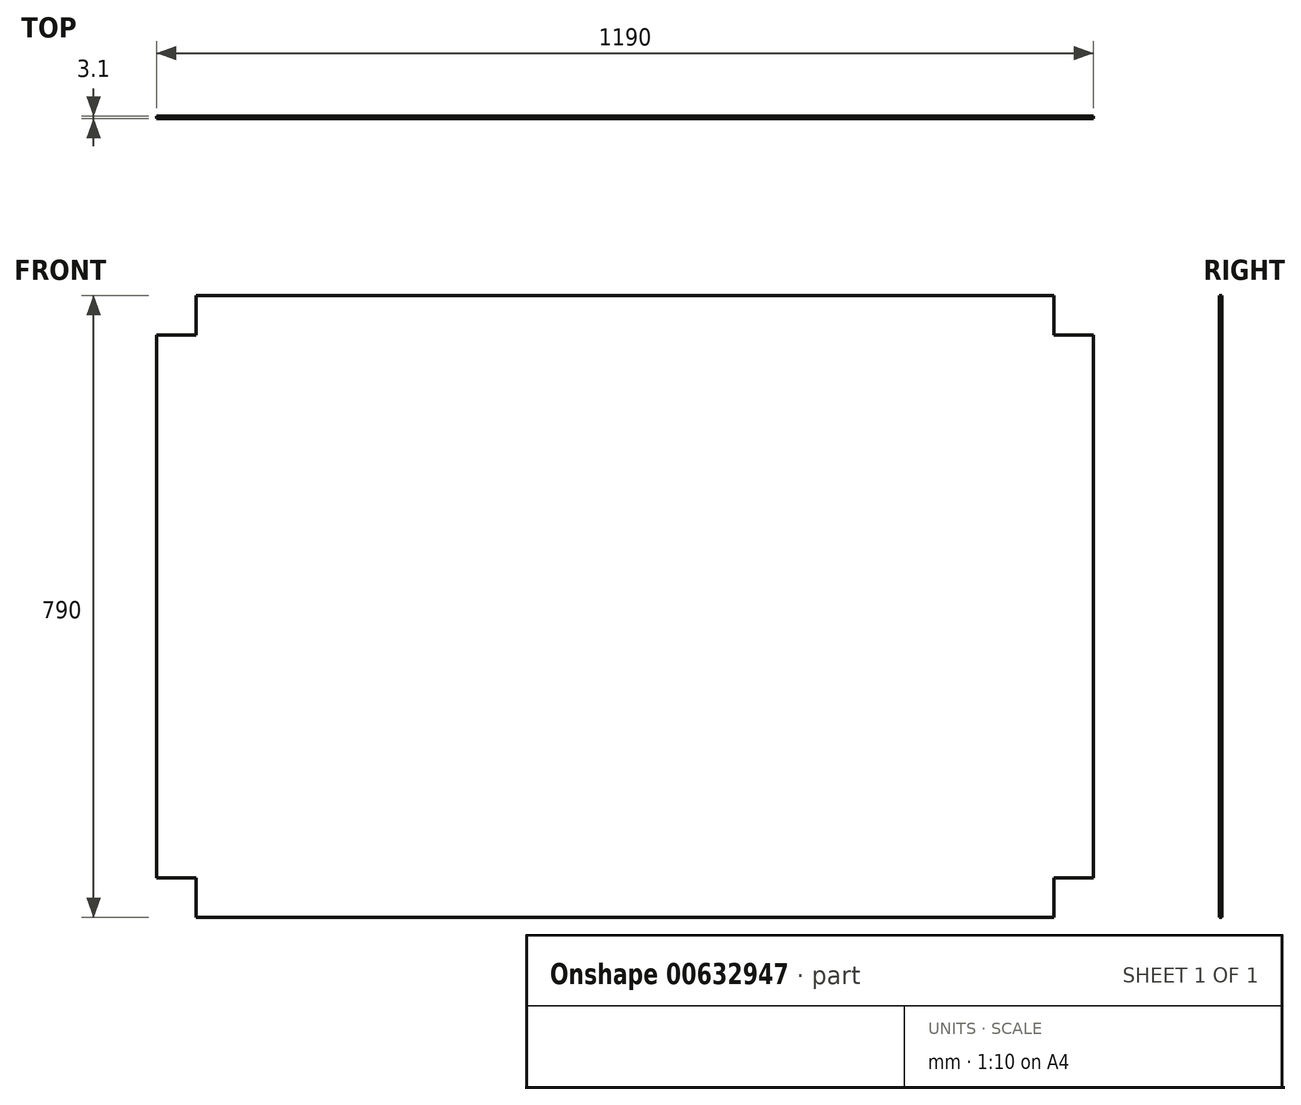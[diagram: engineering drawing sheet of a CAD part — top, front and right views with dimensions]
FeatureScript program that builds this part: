
annotation { "Feature Type Name" : "Feature", "Feature Type Description" : "" }
export const myFeature = defineFeature(function(context is Context, id is Id, definition is map)
    precondition{}
    {
        {
            var Q0;
            Q0=qCreatedBy(makeId("Front.planeOp"),FACE);
            var sketch = newSketch(context, id + "F0", { "sketchPlane" : qUnion([Q0])});
            skLineSegment(sketch, "E0", {"start": v(0, 0) * mm, "end": v(0, -690) * mm});
            skLineSegment(sketch, "E1", {"start": v(0, -690) * mm, "end": v(50, -690) * mm});
            skLineSegment(sketch, "E2", {"start": v(50, -690) * mm, "end": v(50, -740) * mm});
            skLineSegment(sketch, "E3", {"start": v(50, -740) * mm, "end": v(1140, -740) * mm});
            skLineSegment(sketch, "E4", {"start": v(1140, -740) * mm, "end": v(1140, -690) * mm});
            skLineSegment(sketch, "E5", {"start": v(1140, -690) * mm, "end": v(1190, -690) * mm});
            skLineSegment(sketch, "E6", {"start": v(1190, -690) * mm, "end": v(1190, 0) * mm});
            skLineSegment(sketch, "E7", {"start": v(1190, 0) * mm, "end": v(1140, 0) * mm});
            skLineSegment(sketch, "E8", {"start": v(1140, 0) * mm, "end": v(1140, 50) * mm});
            skLineSegment(sketch, "E9", {"start": v(1140, 50) * mm, "end": v(50, 50) * mm});
            skLineSegment(sketch, "E10", {"start": v(50, 50) * mm, "end": v(50, 0) * mm});
            skLineSegment(sketch, "E11", {"start": v(50, 0) * mm, "end": v(0, 0) * mm});
            skSolve(sketch);
        }
        {
            var Q0;
            Q0=makeQuery(id+"F0.imprint","IMPRINT",FACE,{"disambiguationData":[TD([[makeQuery(id+"F0.imprint","IMPRINT",EDGE,{"derivedFrom":sQuery(id+"F0.wireOp",EDGE,"E0")}),1.0]])]});
            extrude(context, id + "F1", {"entities" : qUnion([Q0]), "depth" : 3.1 * mm, "offsetDistance" : 25 * mm});
        }
    });
